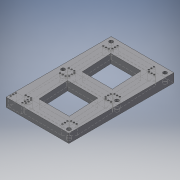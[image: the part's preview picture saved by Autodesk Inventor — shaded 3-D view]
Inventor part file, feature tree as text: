
AUTODESK INVENTOR PART (.ipt)
format: ipt  version: 2016 SP2 (Build 200236200, 236)  size: 749,568 bytes
history: native  units: mm
features: reference x21, extrude x12, sketch x12, projected_geometry x5, chamfer x1
ambient origin geometry x8: Origin, YZ Plane, XZ Plane, XY Plane, X Axis, Y Axis, Z Axis, Center Point
bodies: Volumenkörper1 (feature_tree)
feature tree (51):
  extrude  "Extrusion1"  Depth=0.2mm
  extrude  "Extrusion2"  Depth=0.2mm
  extrude  "Extrusion3"  Depth=0.2mm
  extrude  "Extrusion4"  Depth=0.2mm
  extrude  "Extrusion5"  Depth=0.2mm
  extrude  "Extrusion6"  Depth=0.2mm
  chamfer  "Fase1"  Distance=10.4mm
  extrude  "Extrusion7"  Depth=10.4mm
  extrude  "Extrusion8"  Depth=50.4mm
  extrude  "Extrusion9"  Depth=0.2mm
  extrude  "Extrusion10"  Depth=0.2mm
  extrude  "Extrusion11"  Depth=0.2mm
  extrude  "Extrusion12"  TaperAngle=90.0deg  [1 undecoded]
  sketch  "Skizze1"  dims[d0=0.2mm d1=0.2mm]
  reference  "Referenz1"
  reference  "Referenz2"
  reference  "Referenz3"
  reference  "Referenz4"
  reference  "Referenz5"
  reference  "Referenz6"
  reference  "Referenz7"
  reference  "Referenz8"
  reference  "Referenz9"
  reference  "Referenz10"
  reference  "Referenz11"
  reference  "Referenz12"
  reference  "Referenz13"
  reference  "Referenz14"
  sketch  "Skizze2"  dims[d2=0.2mm d3=0.2mm]
  reference  "Referenz15"
  reference  "Referenz16"
  projected_geometry  "Projizierte Kontur1"
  sketch  "Skizze3"  dims[d4=0.2mm d5=0.2mm]
  reference  "Referenz17"
  sketch  "Skizze4"  dims[d6=0.2mm d7=0.2mm]
  sketch  "Skizze5"  dims[d8=0.2mm d9=0.2mm]
  projected_geometry  "Projizierte Kontur2"
  projected_geometry  "Projizierte Kontur3"
  sketch  "Skizze6"  dims[d10=0.2mm d11=0.2mm]
  projected_geometry  "Projizierte Kontur4"
  projected_geometry  "Projizierte Kontur5"
  sketch  "Skizze7"  dims[d12=0.2mm]
  sketch  "Skizze8"  dims[d13=0.2mm]
  sketch  "Skizze9"  dims[d14=0.2mm d16=10.4mm d17=10.4mm]
  reference  "Referenz18"
  reference  "Referenz19"
  reference  "Referenz20"
  reference  "Referenz21"
  sketch  "Skizze10"  dims[d18=10.4mm d19=10.4mm]
  sketch  "Skizze12"  dims[d20=50.4mm d21=50.4mm d22=50.4mm]
  sketch  "Skizze13"  dims[d23=50.4mm d24=0.2mm d25=0.2mm d26=0.2mm d28=90.0deg d29=50.4mm d30=0.2mm d31=0.2mm d32=10.4mm d33=11.0mm d34=0.0mm d35=17.0mm d36=11.0mm d37=5.5mm d38=1.2mm d39=0.282455mm d40=0.282455mm d41=0.282455mm d42=0.282455mm d43=0.282455mm d44=0.282455mm d45=0.282455mm d46=9.0mm d47=0.0mm d49=5.0mm d50=5.0mm d51=5.0mm d52=5.0mm d54=5.0mm d56=5.0mm d57=5.0mm d58=5.0mm d59=11.0mm d60=5.5mm d61=1.2mm d62=17.0mm d63=1.2mm d64=11.0mm d65=0.0mm d66=11.0mm d67=17.0mm d68=4.0mm d69=0.0mm d70=2.0mm d71=0.0mm d72=1.5mm d73=0.0mm d74=1.5mm d75=2.0mm d76=45.0deg d77=1.0mm d78=0.0mm d79=0.5mm d80=0.5mm d81=0.5mm d82=0.5mm d83=0.5mm d84=0.5mm d85=0.5mm d86=0.5mm d87=0.5mm d88=0.5mm d89=0.5mm d90=0.5mm d91=0.5mm d92=0.5mm d93=0.5mm d94=0.5mm d95=2.0mm d96=2.0mm d97=2.0mm d98=2.0mm d99=2.0mm d100=2.0mm d101=2.0mm d102=2.0mm d103=2.0mm d104=2.0mm d105=2.0mm d106=2.0mm d107=2.0mm d108=2.0mm d109=2.0mm d110=2.0mm d111=2.0mm d112=2.0mm d113=2.0mm d114=2.0mm d115=2.0mm d116=2.0mm d117=2.0mm d118=2.0mm d119=2.0mm d120=2.0mm d121=2.0mm d122=2.0mm d123=2.0mm d124=2.0mm d125=2.0mm d126=2.0mm d127=2.0mm d128=2.0mm d129=2.0mm d130=2.0mm d131=2.0mm d132=2.0mm d133=2.0mm d134=2.0mm d135=2.0mm d136=2.0mm d137=2.0mm d138=2.0mm d139=2.0mm d140=2.0mm d141=2.0mm d142=2.0mm d143=3.5mm d144=3.5mm d145=3.5mm d146=3.5mm d147=3.5mm d148=3.5mm d149=3.5mm d150=3.5mm d151=3.5mm d152=3.5mm d153=3.5mm d154=3.5mm d155=3.5mm d156=3.5mm d157=3.5mm d158=3.5mm d159=3.5mm d160=3.5mm d161=3.5mm d162=3.5mm d163=3.5mm d164=3.5mm d165=3.5mm d166=3.5mm d167=3.5mm d168=3.5mm d169=3.5mm d170=3.5mm d171=3.5mm d172=3.5mm d173=3.5mm d174=3.5mm d175=1.0mm d176=0.0mm d177=5.0mm d178=5.0mm d179=5.0mm d180=5.0mm d181=5.0mm d182=6.0mm d183=6.0mm d184=6.0mm d185=6.0mm d186=6.0mm d187=6.0mm d188=71.34569mm d189=71.34569mm d190=5.0mm d191=5.0mm d192=3.0mm d193=0.0mm d194=3.0mm d195=0.0mm d197=0.2mm d198=0.2mm d199=0.2mm d200=0.2mm d201=0.2mm d202=0.2mm d203=0.2mm d204=0.2mm d205=0.2mm d206=0.2mm d207=0.2mm d208=0.2mm d209=0.2mm d210=0.2mm d211=9.0mm d212=0.0mm d213=0.2mm d214=0.2mm d215=7.0mm d216=0.0mm]
note: 1 required parameter value undecoded (feature->parameter linkage not recoverable at this tier; creation-order binding heuristic only, values carry confidence <= 0.55)
